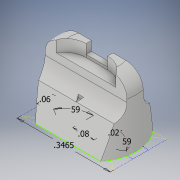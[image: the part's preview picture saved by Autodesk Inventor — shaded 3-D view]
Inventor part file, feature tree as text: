
AUTODESK INVENTOR PART (.ipt)
format: ipt  version: 2018.3 (Build 223284000, 284)  size: 195,072 bytes
history: native  units: in
note: dims shown in document units (in); Inventor stores cm internally (conversion verified against a paired STEP export)
features: extrude x6, sketch x2, chamfer x2, fillet x2, plane x1
ambient origin geometry x8: Origin, YZ Plane, XZ Plane, XY Plane, X Axis, Y Axis, Z Axis, Center Point
bodies: Solid1 (feature_tree)
feature tree (13):
  sketch  "Sketch1"  dims[d0=0.31in d1=0.3465in]
  extrude  "Extrusion1"  Depth=0.3465in
  extrude  "Extrusion2"  Depth=0.045in
  chamfer  "Chamfer1"  Distance=0.115in
  chamfer  "Chamfer2"  Distance=0.245in
  fillet  "Fillet1"  Radius=0.115in
  fillet  "Fillet2"  Radius=0.115in
  plane  "Work Plane2"
  extrude  "Extrusion3"  Depth=0.045in
  extrude  "Extrusion4"  Depth=0.045in
  extrude  "Extrusion5"  [1 undecoded]
  extrude  "Extrusion6"  TaperAngle=120.0deg  [1 undecoded]
  sketch  "Sketch2"  dims[d2=0.06in d3=0.08in d4=0.115in d5=0.0in d6=0.245in d7=0.0in d8=0.115in d9=0.125in d10=15.0deg d11=0.115in d12=0.125in d13=15.0deg d14=0.0625in d15=0.0625in d17=-0.115in d20=120.0deg d21=0.0575in d22=0.0in d23=0.045in d24=0.0in d25=0.02in d26=0.21in d27=0.0in d34=0.085in d35=0.0in d37=0.4054in d38=0.4054in]
note: 2 required parameter values undecoded (feature->parameter linkage not recoverable at this tier; creation-order binding heuristic only, values carry confidence <= 0.55)
